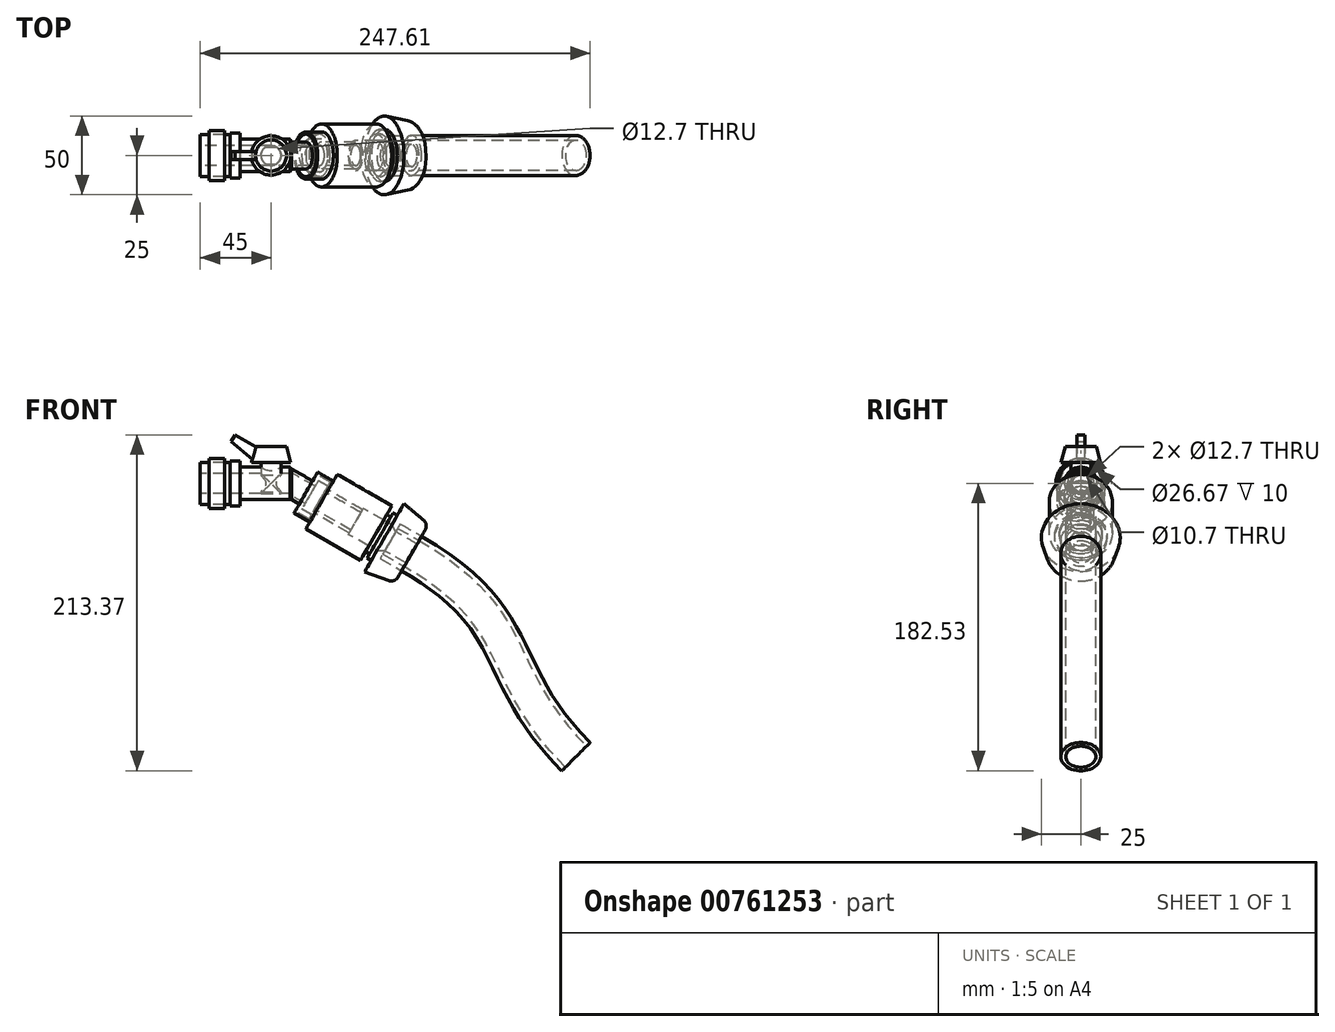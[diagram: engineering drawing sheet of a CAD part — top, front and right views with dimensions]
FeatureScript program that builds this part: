
annotation { "Feature Type Name" : "Feature", "Feature Type Description" : "" }
export const myFeature = defineFeature(function(context is Context, id is Id, definition is map)
    precondition{}
    {
        {
            var Q0;
            Q0=qCreatedBy(makeId("Front.planeOp"),FACE);
            var sketch = newSketch(context, id + "F0", { "sketchPlane" : qUnion([Q0])});
            skLineSegment(sketch, "E0", {"start": v(-106.44, 0) * mm, "end": v(0, 0) * mm, "construction": true});
            skLineSegment(sketch, "E1", {"start": v(0, 0) * mm, "end": v(104.85, -60.53) * mm, "construction": true});
            skLineSegment(sketch, "E2", {"start": v(-57.15, 6.35) * mm, "end": v(-57.15, 13.33) * mm});
            skLineSegment(sketch, "E3", {"start": v(-57.15, 13.33) * mm, "end": v(-38.1, 13.33) * mm});
            skLineSegment(sketch, "E4", {"start": v(-38.1, 13.33) * mm, "end": v(-38.1, 14.34) * mm});
            skLineSegment(sketch, "E5", {"start": v(-38.1, 14.34) * mm, "end": v(-31.75, 14.34) * mm});
            skLineSegment(sketch, "E6", {"start": v(10.23, 3.9) * mm, "end": v(14.24, 1.59) * mm});
            skLineSegment(sketch, "E7", {"start": v(14.24, 1.59) * mm, "end": v(16.74, 5.92) * mm});
            skLineSegment(sketch, "E8", {"start": v(16.74, 5.92) * mm, "end": v(25.4, 0.92) * mm});
            skLineSegment(sketch, "E9", {"start": v(25.4, 0.92) * mm, "end": v(23.9, -1.68) * mm});
            skLineSegment(sketch, "E10", {"start": v(-31.75, 14.34) * mm, "end": v(-31.75, 10.34) * mm});
            skLineSegment(sketch, "E11", {"start": v(-31.75, 10.34) * mm, "end": v(0, 10.34) * mm});
            skLineSegment(sketch, "E12", {"start": v(-57.15, 6.35) * mm, "end": v(0, 6.35) * mm});
            skLineSegment(sketch, "E13", {"start": v(9.15, 2.05) * mm, "end": v(15.77, -1.77) * mm});
            skLineSegment(sketch, "E14", {"start": v(0, 10.34) * mm, "end": v(0, 6.35) * mm});
            skLineSegment(sketch, "E15", {"start": v(15.77, -1.77) * mm, "end": v(17.84, 1.82) * mm});
            skLineSegment(sketch, "E16", {"start": v(17.84, 1.82) * mm, "end": v(23.9, -1.68) * mm});
            skLineSegment(sketch, "E17", {"start": v(2.8, -8.95) * mm, "end": v(9.15, 2.05) * mm, "construction": true});
            skLineSegment(sketch, "E18", {"start": v(0, 6.35) * mm, "end": v(0, -6.35) * mm, "construction": true});
            skLineSegment(sketch, "E19", {"start": v(9.15, 2.05) * mm, "end": v(10.23, 3.9) * mm});
            skLineSegment(sketch, "E20", {"start": v(0, -6.35) * mm, "end": v(0, -10.34) * mm, "construction": true});
            skPoint(sketch, "E21", {"position": v(5.98, -3.45) * mm});
            skLineSegment(sketch, "E22", {"start": v(2.8, -8.95) * mm, "end": v(1.73, -10.8) * mm, "construction": true});
            skLineSegment(sketch, "E23", {"start": v(1.73, -10.8) * mm, "end": v(0, -9.8) * mm, "construction": true});
            skLineSegment(sketch, "E24", {"start": v(9.15, 2.05) * mm, "end": v(0, 7.33) * mm, "construction": true});
            skLineSegment(sketch, "E25", {"start": v(10.23, 3.9) * mm, "end": v(0, 9.8) * mm, "construction": true});
            skLineSegment(sketch, "E26", {"start": v(2.8, -8.95) * mm, "end": v(0, -7.33) * mm, "construction": true});
            skLineSegment(sketch, "E27", {"start": v(16.74, 5.92) * mm, "end": v(17.5, 7.22) * mm});
            skLineSegment(sketch, "E28", {"start": v(17.5, 7.22) * mm, "end": v(27.46, 1.47) * mm});
            skLineSegment(sketch, "E29", {"start": v(27.46, 1.47) * mm, "end": v(24.2, -4.17) * mm});
            skLineSegment(sketch, "E30", {"start": v(24.2, -4.17) * mm, "end": v(45.86, -16.67) * mm});
            skLineSegment(sketch, "E31", {"start": v(45.86, -16.67) * mm, "end": v(44.78, -18.52) * mm});
            skLineSegment(sketch, "E32", {"start": v(44.78, -18.52) * mm, "end": v(21.83, -5.27) * mm});
            skLineSegment(sketch, "E33", {"start": v(21.83, -5.27) * mm, "end": v(23.9, -1.68) * mm});
            skLineSegment(sketch, "E34", {"start": v(23.9, -1.68) * mm, "end": v(25.2, -2.43) * mm, "construction": true});
            skLineSegment(sketch, "E35", {"start": v(27.46, 1.47) * mm, "end": v(29.96, 5.8) * mm});
            skLineSegment(sketch, "E36", {"start": v(29.96, 5.8) * mm, "end": v(64.6, -14.2) * mm});
            skLineSegment(sketch, "E37", {"start": v(64.6, -14.2) * mm, "end": v(61.36, -19.8) * mm});
            skLineSegment(sketch, "E38", {"start": v(61.36, -19.8) * mm, "end": v(63.96, -21.3) * mm});
            skLineSegment(sketch, "E39", {"start": v(63.96, -21.3) * mm, "end": v(65.46, -18.71) * mm});
            skLineSegment(sketch, "E40", {"start": v(65.46, -18.71) * mm, "end": v(68.06, -20.21) * mm});
            skLineSegment(sketch, "E41", {"start": v(68.06, -20.21) * mm, "end": v(72.3, -12.87) * mm});
            skLineSegment(sketch, "E42", {"start": v(72.3, -12.87) * mm, "end": v(87.85, -25.93) * mm});
            skLineSegment(sketch, "E43", {"start": v(87.85, -25.93) * mm, "end": v(83.47, -33.52) * mm});
            skLineSegment(sketch, "E44", {"start": v(81.88, -36.27) * mm, "end": v(68.3, -28.44) * mm});
            skLineSegment(sketch, "E45", {"start": v(45.86, -16.67) * mm, "end": v(46.37, -15.77) * mm});
            skLineSegment(sketch, "E46", {"start": v(61.36, -19.8) * mm, "end": v(59.36, -23.27) * mm});
            skLineSegment(sketch, "E47", {"start": v(81.88, -36.27) * mm, "end": v(80.63, -38.44) * mm});
            skLineSegment(sketch, "E48", {"start": v(80.63, -38.44) * mm, "end": v(67.06, -30.6) * mm});
            skLineSegment(sketch, "E49", {"start": v(67.06, -30.6) * mm, "end": v(64.56, -26.27) * mm});
            skLineSegment(sketch, "E50", {"start": v(68.3, -28.44) * mm, "end": v(69.9, -25.69) * mm});
            skLineSegment(sketch, "E51", {"start": v(69.9, -25.69) * mm, "end": v(83.47, -33.52) * mm});
            skLineSegment(sketch, "E52.trimOffspring", {"start": v(64.56, -26.27) * mm, "end": v(46.37, -15.77) * mm});
            skLineSegment(sketch, "E53", {"start": v(-41.6, 13.33) * mm, "end": v(-41.6, 15.88) * mm});
            skLineSegment(sketch, "E54", {"start": v(-41.6, 15.88) * mm, "end": v(-51.6, 15.88) * mm});
            skLineSegment(sketch, "E55", {"start": v(-51.6, 15.88) * mm, "end": v(-51.6, 13.33) * mm});
            skSolve(sketch);
        }
        {
            var Q0;
            Q0=makeQuery(id+"F0.imprint","IMPRINT",FACE,{"disambiguationData":[TD([[makeQuery(id+"F0.imprint","IMPRINT",EDGE,{"derivedFrom":sQuery(id+"F0.wireOp",EDGE,"E2")}),-1.0]])]});
            var Q1;
            Q1=sQuery(id+"F0.wireOp",EDGE,"E0");
            revolve(context, id + "F1", {"surfaceOperationType" : NewSurfaceOperationType.NEW, "entities" : qUnion([Q0]), "axis" : qUnion([Q1]), "revolveType" : RevolveType.FULL});
        }
        {
            var Q0;
            Q0=makeQuery(id+"F0.imprint","IMPRINT",FACE,{"disambiguationData":[TD([[makeQuery(id+"F0.imprint","IMPRINT",EDGE,{"derivedFrom":sQuery(id+"F0.wireOp",EDGE,"E6")}),-1.0]])]});
            var Q1;
            Q1=sQuery(id+"F0.wireOp",EDGE,"E1");
            revolve(context, id + "F2", {"operationType" : NewBodyOperationType.ADD, "surfaceOperationType" : NewSurfaceOperationType.NEW, "entities" : qUnion([Q0]), "axis" : qUnion([Q1]), "revolveType" : RevolveType.FULL});
        }
        {
            var Q0;
            Q0=makeQuery(id+"F2.opRevolve","SWEPT_FACE",FACE,{"disambiguationData":[OSD([sQuery(id+"F0.wireOp",EDGE,"E19")])]});
            var Q1;
            Q1=makeQuery(id+"F1.opRevolve","SWEPT_FACE",FACE,{"disambiguationData":[OSD([sQuery(id+"F0.wireOp",EDGE,"E14")])]});
            extrude(context, id + "F3", {"entities" : qUnion([Q0]), "operationType" : NewBodyOperationType.ADD, "endBound" : BoundingType.UP_TO_SURFACE, "depth" : 25 * mm, "endBoundEntityFace" : qUnion([Q1]), "hasOffset" : true, "offsetDistance" : 1 * mm});
        }
        {
            var Q0;
            Q0=makeQuery(id+"F1.opRevolve","SWEPT_FACE",FACE,{"disambiguationData":[OSD([sQuery(id+"F0.wireOp",EDGE,"E14")])]});
            var sketch = newSketch(context, id + "F4", { "sketchPlane" : qUnion([Q0])});
            skCircle(sketch, "E56.0", {"center": v(0, 0) * mm, "radius": 10.34 * mm});
            skSolve(sketch);
        }
        {
            var Q0;
            Q0=makeQuery(id+"F3.opExtrude","CAP_FACE",FACE,{"disambiguationData":[OSD([sQuery(id+"F0.wireOp",EDGE,"E19")])],"isStart":false});
            var sketch = newSketch(context, id + "F5", { "sketchPlane" : qUnion([Q0])});
            skEllipse(sketch, "E57.0", {"center": v(0, -0.5) * mm, "majorRadius": 8.9 * mm, "minorRadius": 7.72 * mm, "majorAxis": v(0, -1)});
            skSolve(sketch);
        }
        {
            var Q0;
            Q0=makeQuery(id+"F4.imprint","IMPRINT",FACE,{"disambiguationData":[TD([[makeQuery(id+"F4.imprint","IMPRINT",EDGE,{"derivedFrom":sQuery(id+"F4.wireOp",EDGE,"E56.0")}),-1.0]])]});
            var sketch = newSketch(context, id + "F6", { "sketchPlane" : qUnion([Q0])});
            skCircle(sketch, "E58.0", {"center": v(0, 0) * mm, "radius": 6.35 * mm});
            skSolve(sketch);
        }
        {
            var Q0;
            Q0=makeQuery(id+"F5.imprint","IMPRINT",FACE,{"disambiguationData":[TD([[makeQuery(id+"F5.imprint","IMPRINT",EDGE,{"derivedFrom":sQuery(id+"F5.wireOp",EDGE,"E57.0")}),-1.0]])]});
            var sketch = newSketch(context, id + "F7", { "sketchPlane" : qUnion([Q0])});
            skEllipse(sketch, "E59.0", {"center": v(0, -0.5) * mm, "majorRadius": 6.6 * mm, "minorRadius": 5.71 * mm, "majorAxis": v(0, -1)});
            skSolve(sketch);
        }
        {
            var Q2;
            Q2 = qSketchRegion(id + "F4", true);
            var Q3;
            Q3 = qSketchRegion(id + "F5", true);
            loft(context, id + "F8", {"operationType" : NewBodyOperationType.ADD, "sheetProfilesArray" : [{ "sheetProfileEntities" : qUnion([Q2]) }, { "sheetProfileEntities" : qUnion([Q3]) }]});
        }
        {
            var Q1;
            Q1 = qSketchRegion(id + "F6", true);
            var Q2;
            Q2 = qSketchRegion(id + "F7", true);
            loft(context, id + "F9", {"operationType" : NewBodyOperationType.REMOVE, "sheetProfilesArray" : [{ "sheetProfileEntities" : qUnion([Q1]) }, { "sheetProfileEntities" : qUnion([Q2]) }]});
        }
        {
            var Q0;
            Q0=qCreatedBy(makeId("Front.planeOp"),FACE);
            var sketch = newSketch(context, id + "F10", { "sketchPlane" : qUnion([Q0])});
            skLineSegment(sketch, "E60", {"start": v(-12.15, -17.82) * mm, "end": v(-12.15, 25.4) * mm, "construction": true});
            skLineSegment(sketch, "E61", {"start": v(-24.65, 13.34) * mm, "end": v(-21.97, 23.34) * mm});
            skLineSegment(sketch, "E62", {"start": v(-21.97, 23.34) * mm, "end": v(-12.15, 23.34) * mm});
            skLineSegment(sketch, "E63", {"start": v(-12.15, 23.34) * mm, "end": v(-12.15, -6.35) * mm});
            skLineSegment(sketch, "E64", {"start": v(-24.65, 13.34) * mm, "end": v(-18.5, 13.34) * mm});
            skLineSegment(sketch, "E65", {"start": v(-18.5, 13.34) * mm, "end": v(-18.5, -6.35) * mm});
            skLineSegment(sketch, "E66", {"start": v(-18.5, -6.35) * mm, "end": v(-12.15, -6.35) * mm});
            skLineSegment(sketch, "E67", {"start": v(-18.5, 2.08) * mm, "end": v(-5.8, 2.08) * mm, "construction": true});
            skPoint(sketch, "E68", {"position": v(-12.15, 2.08) * mm});
            skSolve(sketch);
        }
        {
            var Q0;
            Q0 = qSketchRegion(id + "F10", true);
            var Q1;
            Q1=sQuery(id+"F10.wireOp",EDGE,"E60");
            revolve(context, id + "F11", {"surfaceOperationType" : NewSurfaceOperationType.NEW, "entities" : qUnion([Q0]), "axis" : qUnion([Q1]), "revolveType" : RevolveType.FULL});
        }
        {
            var Q0;
            Q0=qCreatedBy(makeId("Front.planeOp"),FACE);
            var sketch = newSketch(context, id + "F12", { "sketchPlane" : qUnion([Q0])});
            skLineSegment(sketch, "E69", {"start": v(-20.24, 22.34) * mm, "end": v(-34.96, 30.84) * mm});
            skLineSegment(sketch, "E70", {"start": v(-34.96, 30.84) * mm, "end": v(-37.46, 26.5) * mm});
            skLineSegment(sketch, "E71", {"start": v(-37.46, 26.5) * mm, "end": v(-22.49, 13.94) * mm});
            skLineSegment(sketch, "E72", {"start": v(-20.24, 22.34) * mm, "end": v(-22.49, 13.94) * mm});
            skSolve(sketch);
        }
        {
            var Q0;
            Q0 = qSketchRegion(id + "F12", true);
            extrude(context, id + "F13", {"entities" : qUnion([Q0]), "operationType" : NewBodyOperationType.ADD, "depth" : 5 * mm, "offsetDistance" : 25 * mm, "symmetric" : true});
        }
        {
            var Q0;
            Q0=sQuery(id+"F10.wireOp",VERTEX,"E60.end");
            var Q1;
            Q1=qCreatedBy(makeId("Right.planeOp"),FACE);
            cPlane(context, id + "F14", {"entities" : qUnion([Q0, Q1]), "cplaneType" : CPlaneType.PLANE_POINT, "offset" : 25 * mm, "width" : 150 * mm, "height" : 150 * mm});
        }
        {
            var Q0;
            Q0=makeQuery(id+"F11.opRevolve","SWEPT_BODY",BODY,{"disambiguationData":[OSD([sQuery(id+"F10.wireOp",EDGE,"E61"),sQuery(id+"F10.wireOp",EDGE,"E62"),sQuery(id+"F10.wireOp",EDGE,"E63"),sQuery(id+"F10.wireOp",EDGE,"E64"),sQuery(id+"F10.wireOp",EDGE,"E65"),sQuery(id+"F10.wireOp",EDGE,"E66")])]});
            var Q1;
            Q1=makeQuery(id+"F1.opRevolve","SWEPT_BODY",BODY,{"disambiguationData":[OSD([sQuery(id+"F0.wireOp",EDGE,"E2"),sQuery(id+"F0.wireOp",EDGE,"E3"),sQuery(id+"F0.wireOp",EDGE,"E4"),sQuery(id+"F0.wireOp",EDGE,"E5"),sQuery(id+"F0.wireOp",EDGE,"E10"),sQuery(id+"F0.wireOp",EDGE,"E11"),sQuery(id+"F0.wireOp",EDGE,"E12"),sQuery(id+"F0.wireOp",EDGE,"E14")])]});
            booleanBodies(context, id + "F15", {"operationType" : BooleanOperationType.SUBTRACTION, "tools" : qUnion([Q0]), "targets" : qUnion([Q1]), "keepTools" : true});
        }
        {
            var Q0;
            Q0=qCreatedBy(id+"F14.planeOp",FACE);
            var sketch = newSketch(context, id + "F16", { "sketchPlane" : qUnion([Q0])});
            skCircle(sketch, "E73", {"center": v(0, 0) * mm, "radius": 5.35 * mm});
            skLineSegment(sketch, "E74", {"start": v(6.35, 0) * mm, "end": v(-6.35, 0) * mm, "construction": true});
            skSolve(sketch);
        }
        {
            var Q0;
            Q0 = qSketchRegion(id + "F16", true);
            extrude(context, id + "F17", {"entities" : qUnion([Q0]), "operationType" : NewBodyOperationType.REMOVE, "oppositeDirection" : true, "depth" : 25 * mm, "offsetDistance" : 25 * mm, "symmetric" : true});
        }
        {
            var Q0;
            Q0=makeQuery(id+"F11.opRevolve","SWEPT_BODY",BODY,{"disambiguationData":[OSD([sQuery(id+"F10.wireOp",EDGE,"E61"),sQuery(id+"F10.wireOp",EDGE,"E62"),sQuery(id+"F10.wireOp",EDGE,"E63"),sQuery(id+"F10.wireOp",EDGE,"E64"),sQuery(id+"F10.wireOp",EDGE,"E65"),sQuery(id+"F10.wireOp",EDGE,"E66")])]});
            var Q1;
            Q1=makeQuery(id+"F1.opRevolve","SWEPT_BODY",BODY,{"disambiguationData":[OSD([sQuery(id+"F0.wireOp",EDGE,"E2"),sQuery(id+"F0.wireOp",EDGE,"E3"),sQuery(id+"F0.wireOp",EDGE,"E4"),sQuery(id+"F0.wireOp",EDGE,"E5"),sQuery(id+"F0.wireOp",EDGE,"E10"),sQuery(id+"F0.wireOp",EDGE,"E11"),sQuery(id+"F0.wireOp",EDGE,"E12"),sQuery(id+"F0.wireOp",EDGE,"E14"),sQuery(id+"F0.wireOp",EDGE,"fa22ba51-54ec-4944-9d50-440318b9aea1"),sQuery(id+"F0.wireOp",EDGE,"c7fa8621-85da-45d1-9aa6-a5296639682f")])]});
            booleanBodies(context, id + "F18", {"operationType" : BooleanOperationType.SUBTRACTION, "tools" : qUnion([Q0]), "targets" : qUnion([Q1]), "keepTools" : true});
        }
        {
            var Q0;
            Q0=makeQuery(id+"F0.imprint","IMPRINT",FACE,{"disambiguationData":[TD([[makeQuery(id+"F0.imprint","IMPRINT",EDGE,{"derivedFrom":sQuery(id+"F0.wireOp",EDGE,"E8")}),1.0]])]});
            var Q1;
            Q1=sQuery(id+"F0.wireOp",EDGE,"E1");
            revolve(context, id + "F19", {"surfaceOperationType" : NewSurfaceOperationType.NEW, "entities" : qUnion([Q0]), "axis" : qUnion([Q1]), "revolveType" : RevolveType.FULL});
        }
        {
            var Q0;
            Q0=makeQuery(id+"F0.imprint","IMPRINT",FACE,{"disambiguationData":[TD([[makeQuery(id+"F0.imprint","IMPRINT",EDGE,{"derivedFrom":sQuery(id+"F0.wireOp",EDGE,"E29")}),1.0]])]});
            var Q1;
            Q1=sQuery(id+"F0.wireOp",EDGE,"E1");
            revolve(context, id + "F20", {"surfaceOperationType" : NewSurfaceOperationType.NEW, "entities" : qUnion([Q0]), "axis" : qUnion([Q1]), "revolveType" : RevolveType.FULL});
        }
        {
            var Q0;
            Q0=makeQuery(id+"F0.imprint","IMPRINT",FACE,{"disambiguationData":[TD([[makeQuery(id+"F0.imprint","IMPRINT",EDGE,{"derivedFrom":sQuery(id+"F0.wireOp",EDGE,"E38")}),-1.0]])]});
            var Q1;
            Q1=sQuery(id+"F0.wireOp",EDGE,"E1");
            revolve(context, id + "F21", {"surfaceOperationType" : NewSurfaceOperationType.NEW, "entities" : qUnion([Q0]), "axis" : qUnion([Q1]), "revolveType" : RevolveType.FULL});
        }
        {
            var Q0;
            Q0=makeQuery(id+"F21.opRevolve","SWEPT_EDGE",EDGE,{"disambiguationData":[OSD([sQuery(id+"F0.wireOp",EDGE,"E42"),sQuery(id+"F0.wireOp",EDGE,"E43")])]});
            fillet(context, id + "F22", {"entities" : qUnion([Q0]), "radius" : 5 * mm, "tangentPropagation" : true, "allowEdgeOverflow" : false});
        }
        {
            var Q0;
            Q0=qCreatedBy(makeId("Front.planeOp"),FACE);
            var sketch = newSketch(context, id + "F23", { "sketchPlane" : qUnion([Q0])});
            skLineSegment(sketch, "E75", {"start": v(63.54, -36.69) * mm, "end": v(77.12, -44.52) * mm});
            skFitSpline(sketch, "E76", {"points": [v(77.12, -44.52) * mm, v(181.48, -173.55) * mm], "startDerivative": vector(219.85, -126.93) * mm, "endDerivative": vector(160.29, -160.29) * mm});
            skLineSegment(sketch, "E77", {"start": v(93, -85.07) * mm, "end": v(306.46, -298.52) * mm, "construction": true});
            skSolve(sketch);
        }
        {
            var Q0;
            Q0=makeQuery(id+"F21.opRevolve","SWEPT_FACE",FACE,{"disambiguationData":[OSD([sQuery(id+"F0.wireOp",EDGE,"E50")])]});
            var sketch = newSketch(context, id + "F24", { "sketchPlane" : qUnion([Q0])});
            skCircle(sketch, "E78.0", {"center": v(0, 0) * mm, "radius": 9.53 * mm});
            skCircle(sketch, "E78.1", {"center": v(0, 0) * mm, "radius": 12.7 * mm});
            skSolve(sketch);
        }
        {
            var Q0;
            Q0 = qSketchRegion(id + "F24", true);
            var Q1;
            Q1=sQuery(id+"F23.wireOp",EDGE,"E76");
            var Q2;
            Q2=sQuery(id+"F23.wireOp",EDGE,"E75");
            sweep(context, id + "F25", {"profiles" : qUnion([Q0]), "path" : qUnion([Q1, Q2])});
        }
        {
            var Q0;
            {var subQ0=sQuery(id+"F0.wireOp",EDGE,"E53");Q0=makeQuery(id+"F0.imprint","IMPRINT",FACE,{"disambiguationData":[TD([[makeQuery(id+"F0.imprint","IMPRINT",EDGE,{"derivedFrom":subQ0}),1.0]])]});}
            var Q1;
            Q1=sQuery(id+"F0.wireOp",EDGE,"E0");
            revolve(context, id + "F26", {"surfaceOperationType" : NewSurfaceOperationType.NEW, "entities" : qUnion([Q0]), "axis" : qUnion([Q1]), "revolveType" : RevolveType.FULL});
        }
    });
